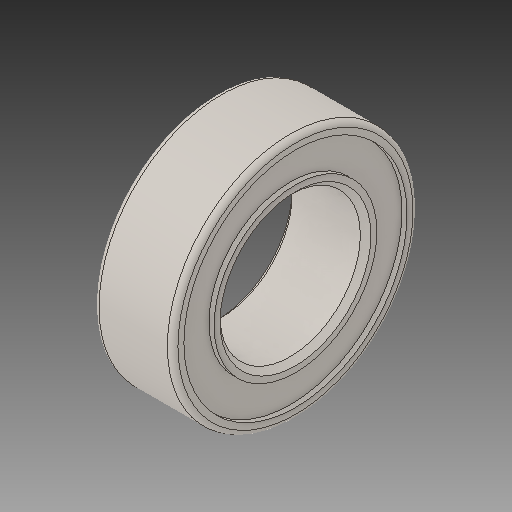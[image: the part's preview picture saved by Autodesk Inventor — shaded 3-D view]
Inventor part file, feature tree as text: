
AUTODESK INVENTOR PART (.ipt)
format: ipt  version: 2017 (Build 210142000, 142)  size: 167,936 bytes
history: native  units: in
note: dims shown in document units (in); Inventor stores cm internally (conversion verified against a paired STEP export)
features: revolve x1
ambient origin geometry x8: Origin, YZ Plane, XZ Plane, XY Plane, X Axis, Y Axis, Z Axis, Center Point
bodies: Solid1 (feature_tree)
feature tree (1):
  revolve  "Revolve1"  [1 undecoded]
note: 1 required parameter value undecoded (feature->parameter linkage not recoverable at this tier; creation-order binding heuristic only, values carry confidence <= 0.55)
